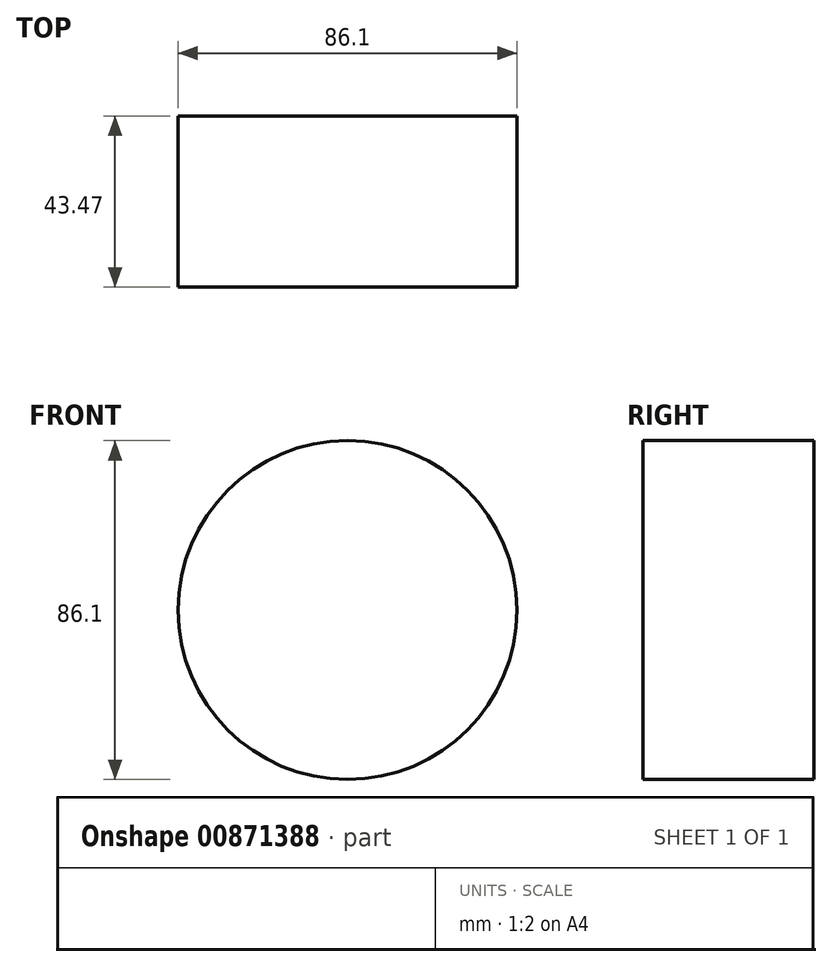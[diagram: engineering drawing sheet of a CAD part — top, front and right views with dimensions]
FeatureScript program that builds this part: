
annotation { "Feature Type Name" : "Feature", "Feature Type Description" : "" }
export const myFeature = defineFeature(function(context is Context, id is Id, definition is map)
    precondition{}
    {
        {
            var Q0;
            Q0=qCreatedBy(makeId("Front.planeOp"),FACE);
            var sketch = newSketch(context, id + "F0", { "sketchPlane" : qUnion([Q0])});
            skCircle(sketch, "E0", {"center": v(0, 0) * mm, "radius": 43.05 * mm});
            skSolve(sketch);
        }
        {
            var Q0;
            Q0=makeQuery(id+"F0.imprint","IMPRINT",FACE,{"disambiguationData":[TD([[makeQuery(id+"F0.imprint","IMPRINT",EDGE,{"derivedFrom":sQuery(id+"F0.wireOp",EDGE,"E0")}),1.0]])]});
            extrude(context, id + "F1", {"entities" : qUnion([Q0]), "depth" : 43.47 * mm, "offsetDistance" : 25.4 * mm});
        }
        {
            var Q0;
            Q0=qCreatedBy(makeId("Front.planeOp"),FACE);
            var sketch = newSketch(context, id + "F2", { "sketchPlane" : qUnion([Q0])});
            skCircle(sketch, "E1", {"center": v(0, 0) * mm, "radius": 26.8 * mm});
            skCircle(sketch, "E2", {"center": v(0, 0) * mm, "radius": 15.6 * mm});
            skSolve(sketch);
        }
        {
            var Q0;
            Q0=sQuery(id+"F2.wireOp",EDGE,"E1");
            extrude(context, id + "F3", {"bodyType" : ToolBodyType.SURFACE, "surfaceEntities" : qUnion([Q0]), "depth" : 73.1 * mm, "offsetDistance" : 25.4 * mm});
        }
        {
            var Q0;
            Q0=qCreatedBy(makeId("Front.planeOp"),FACE);
            var sketch = newSketch(context, id + "F4", { "sketchPlane" : qUnion([Q0])});
            skCircle(sketch, "E3", {"center": v(0, 0) * mm, "radius": 17.55 * mm});
            skSolve(sketch);
        }
        {
            var Q0;
            Q0=sQuery(id+"F4.wireOp",EDGE,"E3");
            extrude(context, id + "F5", {"bodyType" : ToolBodyType.SURFACE, "surfaceEntities" : qUnion([Q0]), "depth" : 92 * mm, "offsetDistance" : 25.4 * mm});
        }
    });
